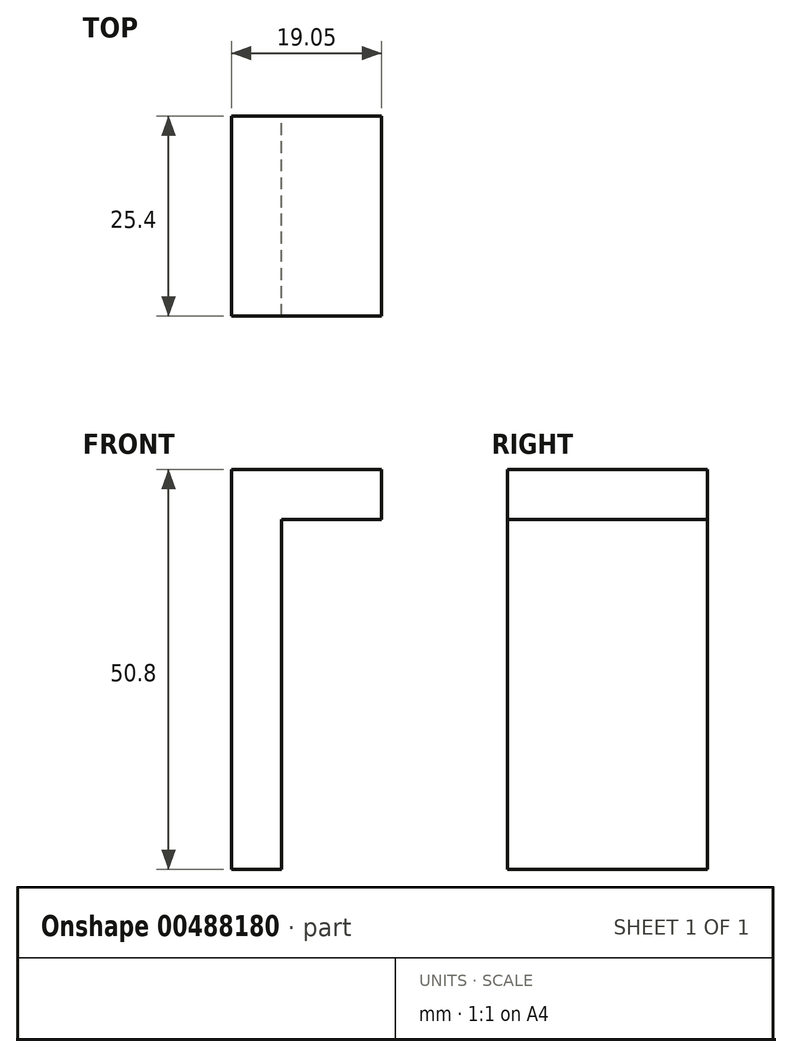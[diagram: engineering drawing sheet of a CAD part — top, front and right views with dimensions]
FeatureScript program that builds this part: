
annotation { "Feature Type Name" : "Feature", "Feature Type Description" : "" }
export const myFeature = defineFeature(function(context is Context, id is Id, definition is map)
    precondition{}
    {
        {
            var Q0;
            Q0=qCreatedBy(makeId("Front.planeOp"),FACE);
            var sketch = newSketch(context, id + "F0", { "sketchPlane" : qUnion([Q0])});
            skLineSegment(sketch, "E0", {"start": v(0, 0) * mm, "end": v(0, 50.8) * mm});
            skLineSegment(sketch, "E1", {"start": v(0, 50.8) * mm, "end": v(19.05, 50.8) * mm});
            skLineSegment(sketch, "E2", {"start": v(19.05, 50.8) * mm, "end": v(19.05, 44.45) * mm});
            skLineSegment(sketch, "E3", {"start": v(19.05, 44.45) * mm, "end": v(6.35, 44.45) * mm});
            skLineSegment(sketch, "E4", {"start": v(6.35, 44.45) * mm, "end": v(6.35, 0) * mm});
            skLineSegment(sketch, "E5", {"start": v(6.35, 0) * mm, "end": v(0, 0) * mm});
            skSolve(sketch);
        }
        {
            var Q0;
            Q0=makeQuery(id+"F0.imprint","IMPRINT",FACE,{"disambiguationData":[TD([[makeQuery(id+"F0.imprint","IMPRINT",EDGE,{"derivedFrom":sQuery(id+"F0.wireOp",EDGE,"E0")}),-1.0]])]});
            extrude(context, id + "F1", {"entities" : qUnion([Q0]), "depth" : 25.4 * mm});
        }
    });
